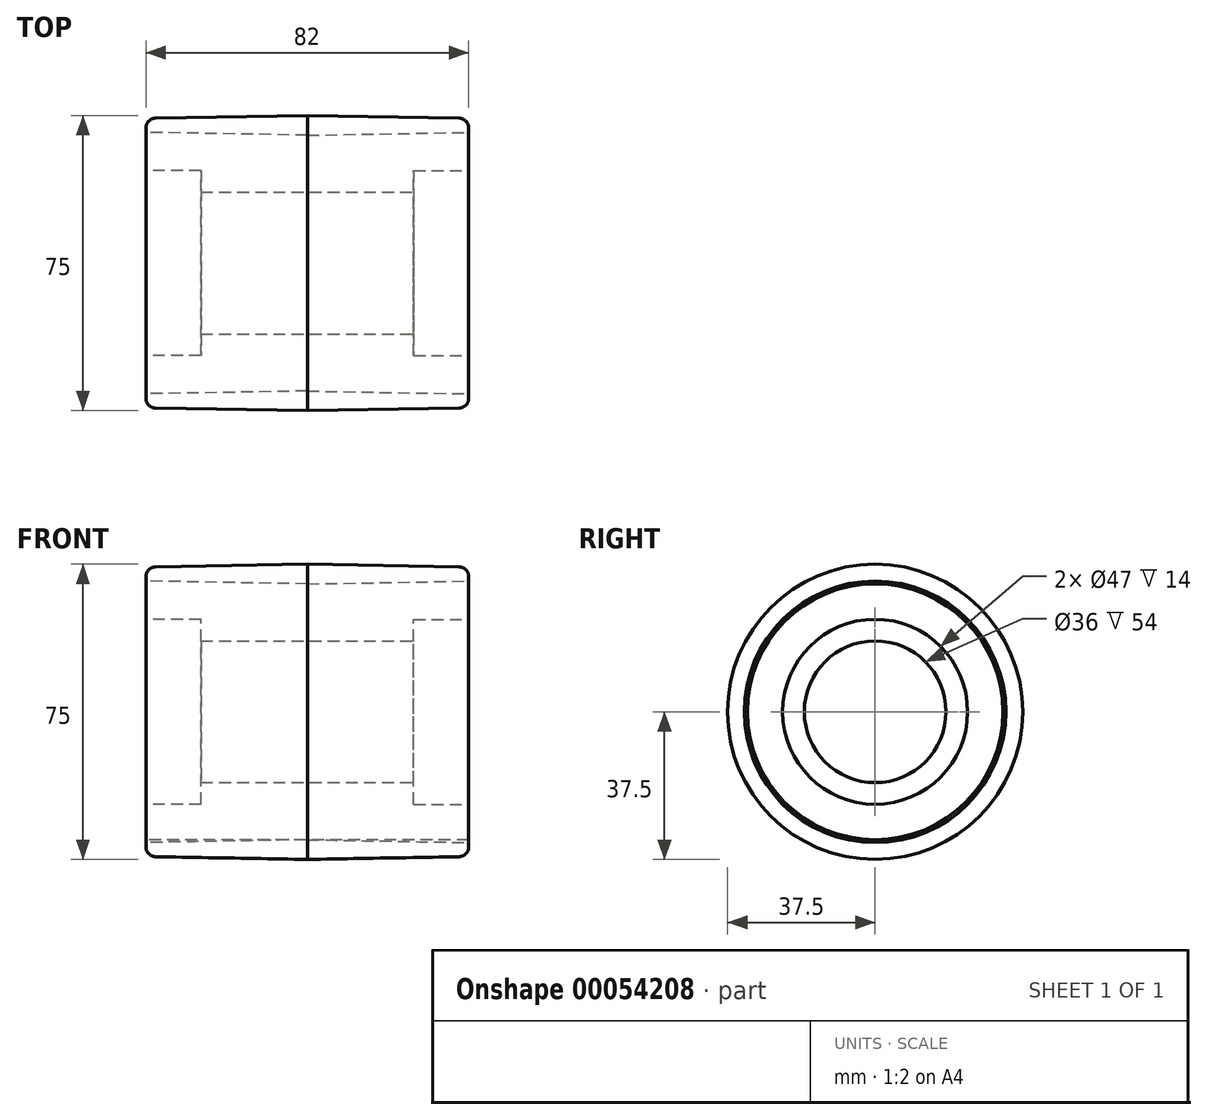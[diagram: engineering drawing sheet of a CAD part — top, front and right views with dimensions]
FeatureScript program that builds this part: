
annotation { "Feature Type Name" : "Feature", "Feature Type Description" : "" }
export const myFeature = defineFeature(function(context is Context, id is Id, definition is map)
    precondition{}
    {
        {
            var Q0;
            Q0=qCreatedBy(makeId("Right.planeOp"),FACE);
            var sketch = newSketch(context, id + "F0", { "sketchPlane" : qUnion([Q0])});
            skCircle(sketch, "E0", {"center": v(0, 0) * mm, "radius": 37.5 * mm});
            skCircle(sketch, "E1.0", {"center": v(0, 0) * mm, "radius": 32.5 * mm});
            skSolve(sketch);
        }
        {
            var Q0;
            Q0=makeQuery(id+"F0.imprint","IMPRINT",FACE,{"disambiguationData":[TD([[makeQuery(id+"F0.imprint","IMPRINT",EDGE,{"derivedFrom":sQuery(id+"F0.wireOp",EDGE,"E0")}),1.0]])]});
            extrude(context, id + "F1", {"entities" : qUnion([Q0]), "endBound" : BoundingType.SYMMETRIC, "depth" : 82 * mm, "hasDraft" : true, "draftAngle" : 1 * degree, "draftPullDirection" : true});
        }
        {
            var Q0;
            Q0=makeQuery(id+"F1.opExtrude","CAP_EDGE",EDGE,{"disambiguationData":[OSD([sQuery(id+"F0.wireOp",EDGE,"E0")])],"isStart":false});
            var Q1;
            Q1=makeQuery(id+"F1.opExtrude","CAP_EDGE",EDGE,{"disambiguationData":[OSD([sQuery(id+"F0.wireOp",EDGE,"E0")])],"isStart":true});
            fillet(context, id + "F2", {"entities" : qUnion([Q0, Q1]), "radius" : 2.5 * mm, "tangentPropagation" : true, "allowEdgeOverflow" : false});
        }
        {
            var Q0;
            Q0=makeQuery(id+"F0.imprint","IMPRINT",FACE,{"disambiguationData":[TD([[makeQuery(id+"F0.imprint","IMPRINT",EDGE,{"derivedFrom":sQuery(id+"F0.wireOp",EDGE,"E1.0")}),1.0]])]});
            extrude(context, id + "F3", {"entities" : qUnion([Q0]), "endBound" : BoundingType.SYMMETRIC, "depth" : 82 * mm});
        }
        {
            var Q0;
            Q0=makeQuery(id+"F3.opExtrude","CAP_FACE",FACE,{"disambiguationData":[OSD([sQuery(id+"F0.wireOp",EDGE,"E1.0")])],"isStart":false});
            var sketch = newSketch(context, id + "F4", { "sketchPlane" : qUnion([Q0])});
            skCircle(sketch, "E2", {"center": v(0, 0) * mm, "radius": 23.5 * mm});
            skSolve(sketch);
        }
        {
            var Q0;
            Q0 = qSketchRegion(id + "F4", true);
            extrude(context, id + "F5", {"entities" : qUnion([Q0]), "operationType" : NewBodyOperationType.REMOVE, "oppositeDirection" : true, "depth" : 14 * mm});
        }
        {
            var Q0;
            Q0=makeQuery(id+"F5.boolean.opBoolean","COPY",FACE,{"derivedFrom":makeQuery(id+"F5.opExtrude","SWEPT_FACE",FACE,{"disambiguationData":[OSD([sQuery(id+"F4.wireOp",EDGE,"E2")])]})});
            var Q1;
            Q1=makeQuery(id+"F5.boolean.opBoolean","COPY",FACE,{"derivedFrom":makeQuery(id+"F5.opExtrude","CAP_FACE",FACE,{"disambiguationData":[OSD([sQuery(id+"F4.wireOp",EDGE,"E2")])],"isStart":false})});
            var Q2;
            Q2=qCreatedBy(makeId("Right.planeOp"),FACE);
            mirror(context, id + "F6", {"faces" : qUnion([Q0, Q1]), "mirrorPlane" : qUnion([Q2]), "patternType" : MirrorType.FACE});
        }
        {
            var Q0;
            Q0=qCreatedBy(makeId("Right.planeOp"),FACE);
            var sketch = newSketch(context, id + "F7", { "sketchPlane" : qUnion([Q0])});
            skCircle(sketch, "E3", {"center": v(0, 0) * mm, "radius": 18 * mm});
            skSolve(sketch);
        }
        {
            var Q0;
            Q0 = qSketchRegion(id + "F7", true);
            extrude(context, id + "F8", {"entities" : qUnion([Q0]), "operationType" : NewBodyOperationType.REMOVE, "endBound" : BoundingType.UP_TO_NEXT, "oppositeDirection" : true, "depth" : 25 * mm, "hasSecondDirection" : true, "secondDirectionBound" : SecondDirectionBoundingType.UP_TO_NEXT, "secondDirectionOppositeDirection" : false, "secondDirectionDepth" : 25 * mm});
        }
    });
